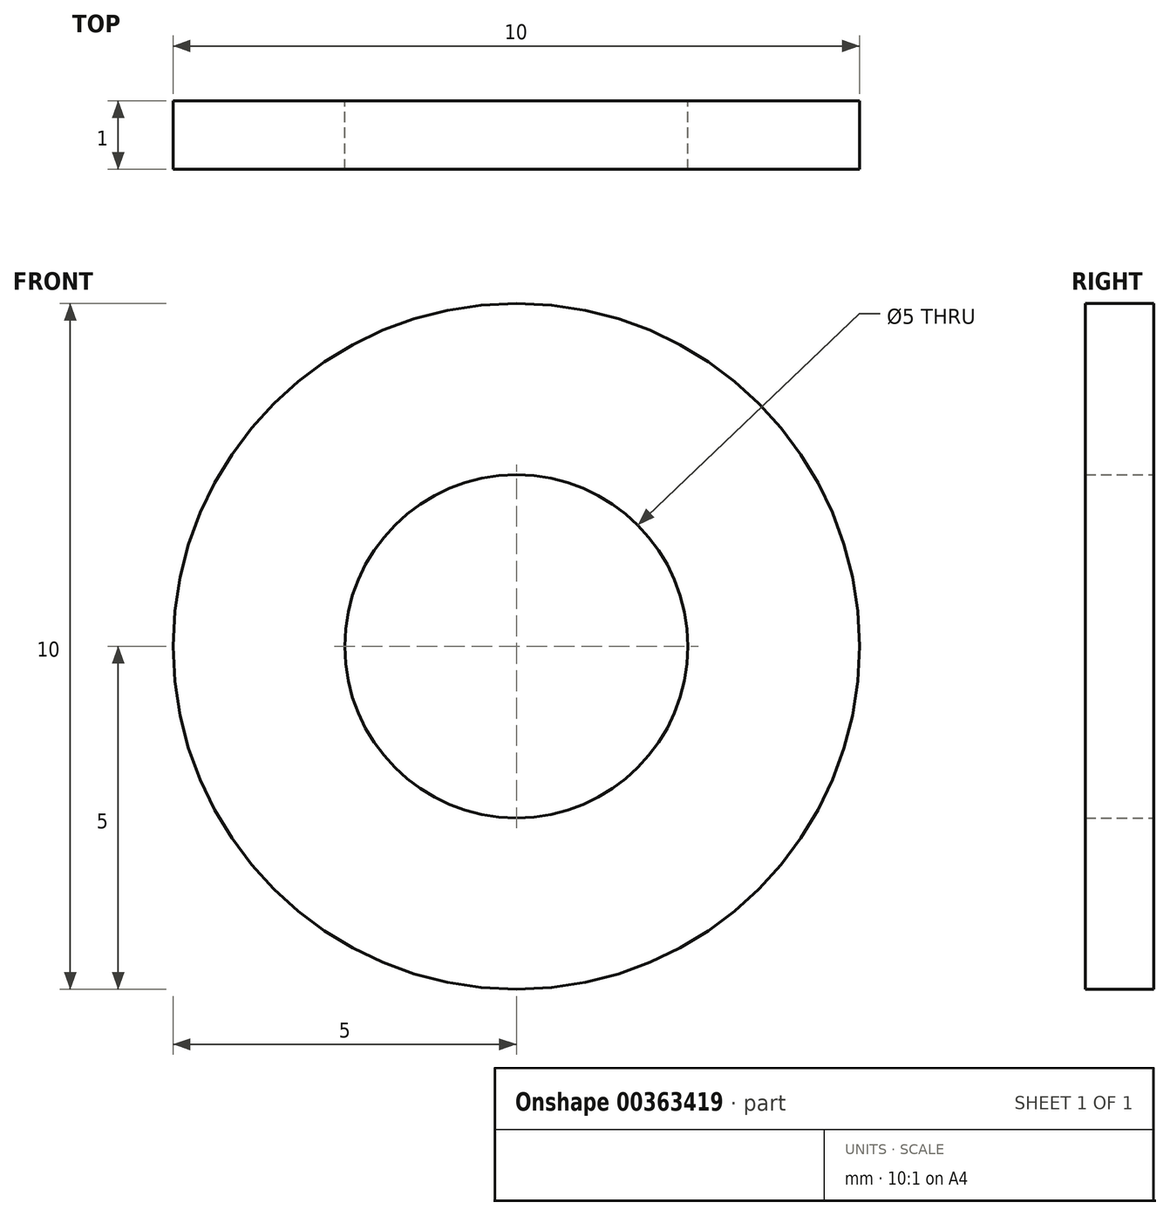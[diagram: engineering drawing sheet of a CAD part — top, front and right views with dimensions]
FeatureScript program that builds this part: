
annotation { "Feature Type Name" : "Feature", "Feature Type Description" : "" }
export const myFeature = defineFeature(function(context is Context, id is Id, definition is map)
    precondition{}
    {
        {
            var Q0;
            Q0=qCreatedBy(makeId("Front.planeOp"),FACE);
            var sketch = newSketch(context, id + "F0", { "sketchPlane" : qUnion([Q0])});
            skCircle(sketch, "E0", {"center": v(0, 0) * mm, "radius": 2.5 * mm});
            skCircle(sketch, "E1", {"center": v(0, 0) * mm, "radius": 5 * mm});
            skSolve(sketch);
        }
        {
            var Q0;
            Q0=makeQuery(id+"F0.imprint","IMPRINT",FACE,{"disambiguationData":[TD([[makeQuery(id+"F0.imprint","IMPRINT",EDGE,{"derivedFrom":sQuery(id+"F0.wireOp",EDGE,"E0")}),-1.0]])]});
            extrude(context, id + "F1", {"entities" : qUnion([Q0]), "depth" : 1 * mm, "offsetDistance" : 25 * mm});
        }
    });
